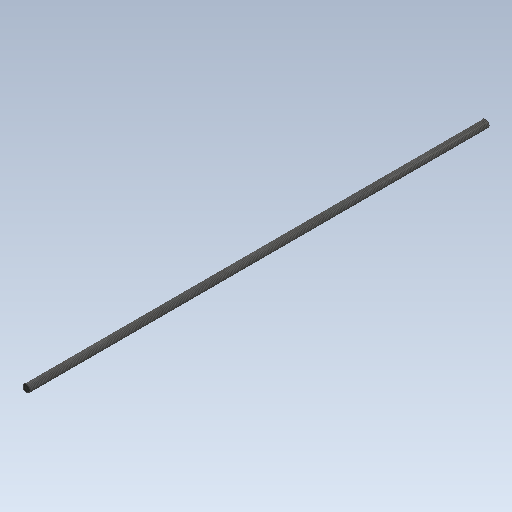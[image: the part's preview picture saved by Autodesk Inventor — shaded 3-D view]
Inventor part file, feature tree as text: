
AUTODESK INVENTOR PART (.ipt)
format: ipt  version: 2020 (Build 240168000, 168)  size: 94,208 bytes
history: native  units: mm
features: extrude x1, thread x1, sketch x1
ambient origin geometry x8: Origin, YZ Plane, XZ Plane, XY Plane, X Axis, Y Axis, Z Axis, Center Point
bodies: Solid1 (feature_tree)
feature tree (3):
  extrude  "Extrusion1"  Depth=500.0mm TaperAngle=0.0deg
  thread  "Thread1"  [1 undecoded]
  sketch  "Sketch1"  dims[d0=8.0mm d1=500.0mm d2=0.0mm d3=200.0mm d4=0.0mm]
note: 1 required parameter value undecoded (feature->parameter linkage not recoverable at this tier; creation-order binding heuristic only, values carry confidence <= 0.55)
